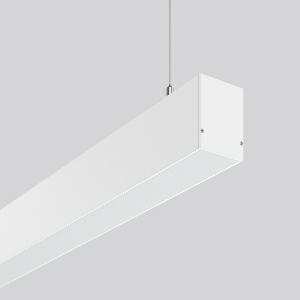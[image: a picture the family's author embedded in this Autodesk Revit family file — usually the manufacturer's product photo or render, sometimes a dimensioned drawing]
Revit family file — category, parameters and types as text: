
# Revit family: less_is_more_50_312320_002_1_76_117a
name_source: partatom
category: Lighting Fixtures
units: mm (PartAtom-declared; Revit-internal decimal feet)

## family parameters
Cut with Voids When Loaded = No
Host = Face
Light Source = No
Part Type = Normal
Room Calculation Point = No
Round Connector Dimension = Use Diameter
Shared = No

## types (1)
- LESS IS MORE 50 (1 x LED Modul 840, 7250 lm, 4000)
    Apparent Load = 59 VA
    CIE Flux Codes = 49 80 96 63 100
    Color Rendering = 80
    Color Temperature = 4000
    Default Elevation = 1800 mm
    Description = Series: LESS IS MORE 50
Linear pendant luminaire for aesthetically sophisticated lighting. Housing: extruded aluminium profile, powder-coated. End cap aluminium powder-coated. Canopy made of aluminium, powder-coated. Diffuser made of non-yellowing plastic (PMMA), opal. Direct 65%, indirect 35% light emission. Suitable for pendant. 2-point steel cable suspension freely positionable and infinitely height-adjustable. Special lengths available on request. LED unit with integrated converter interchangeable and removable. Suitable for through-wiring. With sensors or as a safety luminaire on request. 
Colour: traffic white, matt (RAL 9016)
Length: 1687 mm
Width: 57 mm
Height: 75 mm
Suspension length: 2000 mm
Lamp: LED
Socket: without socket
Colour temperature: 4000K
Colour rendering index (CRI): 80
Light source: LED
Socket lamp2: Without base
Colour temperature: 4000K
System power: 59 W
Rated luminous flux: 7250 lm
Luminous efficiency: 123 lm/W
Control gear: Converter, dimmable, DALI
Control gear: Converter, dimmable, DALI
Protection class: I
Type of protection: IP 20
    Height = 75 mm
    Lamp = 1 x LED Modul 840
    Lamp Light Flux = 7250 lm
    Lamp count = 1
    Length = 1687 mm
    Lifetime = 50000 h
    Luminous efficacy = 123 lm/W
    Manufacturer = RZB
    ModVariant = No
    Model = 312320.002.1.76
    Mounting Place = Ceiling
    Mounting Type = Pendant
    Number of Poles = 1
    OnlyDefault = Yes
    Power Factor = 1
    Product Name = LESS IS MORE 50
    Product group = Pendant LED linear luminaires
    ProductGroupID = 907
    Protection Class = Protection class I
    Protection Degree = IP 20
    RLX_Detail_Level = 1
    RLX_Emergency_Light_Flux = 0 lm
    RLX_Emergency_Type = 0
    RLX_Emergency_Type_DB = No
    RlxData = <blob elided: 31665 chars, md5=6fff96a1>
    Socket = socket
    Standby Power = 0 W
    System Light Flux = 7250 lm
    System Power = 59 W
    Type Comments = Product without accessories
    Type Image = 312318.002.jpg
    URL = http://relux.com
    VarID = ---
    Voltage = 230 V
    Voltage Range = 220-240 V
    Weight = 0.00 kg
    Width = 57 mm

## geometry (parser evidence)
native form markers: Blend x4, Sweep x13
no freeform markers — native parametric forms only
